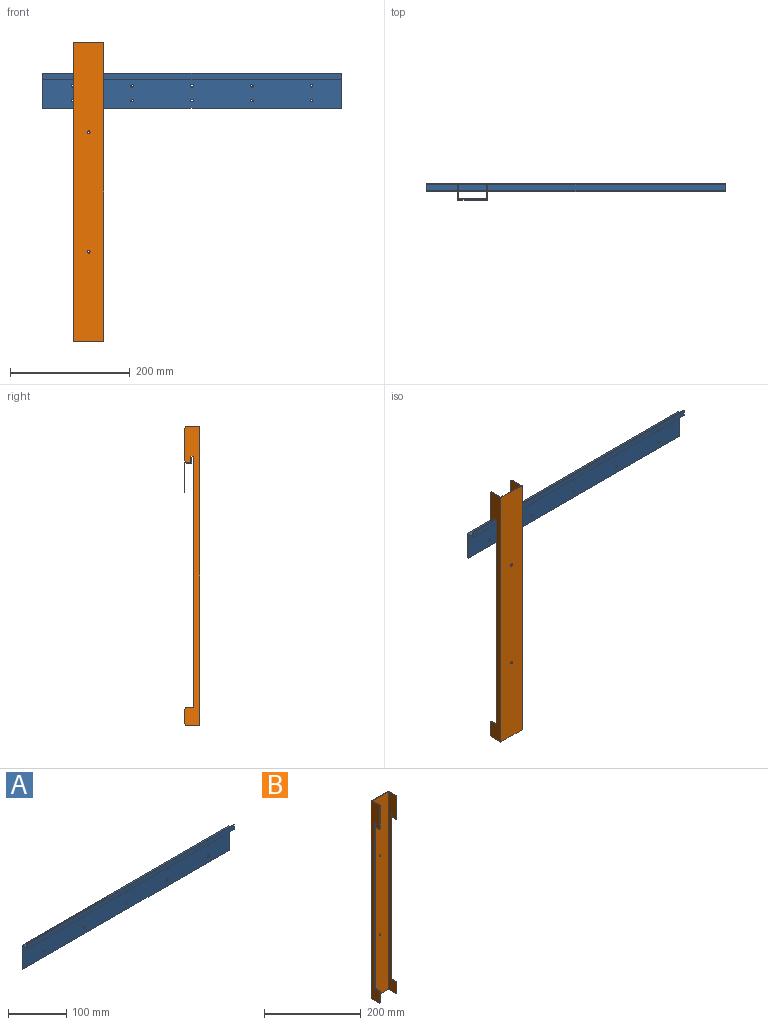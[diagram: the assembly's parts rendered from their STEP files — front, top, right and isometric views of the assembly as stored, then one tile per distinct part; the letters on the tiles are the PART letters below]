
ASSEMBLY  parts=2 mates=1
PART A: 20 faces, bbox 500x13x58.5 mm
  f0: plane 500x11.5mm, normal (0,0,1), area 5750mm2, adj f1,f3,f5,f8
  f1: plane 58.5x13mm, normal (-1,0,0), area 105mm2, adj f0,f2,f4,f5,f6,f7,f8,f9
  f2: plane 500x1.5mm, normal (0,0,-1), area 750mm2, adj f1,f3,f4,f5
  f3: plane 58.5x13mm, normal (1,0,0), area 105mm2, adj f0,f2,f4,f5,f6,f7,f8,f9
  f4: plane 500x48.5mm, normal (0,-1,0), area 24104.8mm2, adj f1,f2,f3,f6,f10,f11,f12,f13
  f5: plane 500x50mm, normal (0,1,0), area 24854.8mm2, adj f0,f1,f2,f3,f10,f11,f12,f13
  f6: plane 500x11.5mm, normal (0,0,-1), area 5750mm2, adj f1,f3,f4,f7
  f7: plane 500x10mm, normal (0,-1,0), area 5000mm2, adj f1,f3,f6,f9
  f8: plane 500x8.5mm, normal (0,1,0), area 4250mm2, adj f0,f1,f3,f9
  f9: plane 500x1.5mm, normal (0,0,1), area 750mm2, adj f1,f3,f7,f8
  f10: cylinder r=2.15mm len=4.3mm, axis (0,-1,0), area 20.3mm2, adj f4,f5
  f11: cylinder r=2.15mm len=4.3mm, axis (0,-1,0), area 20.3mm2, adj f4,f5
  f12: cylinder r=2.15mm len=4.3mm, axis (0,-1,0), area 20.3mm2, adj f4,f5
  f13: cylinder r=2.15mm len=4.3mm, axis (0,-1,0), area 20.3mm2, adj f4,f5
  f14: cylinder r=2.15mm len=4.3mm, axis (0,-1,0), area 20.3mm2, adj f4,f5
  f15: cylinder r=2.15mm len=4.3mm, axis (0,-1,0), area 20.3mm2, adj f4,f5
  f16: cylinder r=2.15mm len=4.3mm, axis (0,-1,0), area 20.3mm2, adj f4,f5
  f17: cylinder r=2.15mm len=4.3mm, axis (0,-1,0), area 20.3mm2, adj f4,f5
  f18: cylinder r=2.15mm len=4.3mm, axis (0,-1,0), area 20.3mm2, adj f4,f5
  f19: cylinder r=2.15mm len=4.3mm, axis (0,-1,0), area 20.3mm2, adj f4,f5
PART B: 32 faces, bbox 50x25x500 mm
  f0: plane 24x1.5mm, normal (0,-1,0), area 36mm2, adj f3,f8,f25,f31
  f1: plane 24x1.5mm, normal (0,-1,0), area 36mm2, adj f5,f10,f27,f28
  f2: plane 500x47mm, normal (0,-1,0), area 23472.3mm2, adj f4,f6,f8,f10,f22,f23
  f3: plane 500x25mm, normal (-1,0,0), area 6292.3mm2, adj f0,f4,f6,f7,f9,f17,f18,f19
  f4: plane 50x22mm, normal (0,0,-1), area 136.5mm2, adj f2,f3,f5,f7,f8,f10,f28,f31
  f5: plane 500x25mm, normal (1,0,0), area 6292.3mm2, adj f1,f4,f6,f7,f11,f12,f13,f14
  f6: plane 50x22mm, normal (0,0,1), area 136.5mm2, adj f2,f3,f5,f7,f8,f10,f29,f30
  f7: plane 500x50mm, normal (0,1,0), area 24972.3mm2, adj f3,f4,f5,f6,f22,f23
  f8: plane 500x23.5mm, normal (1,0,0), area 5542.3mm2, adj f0,f2,f4,f6,f9,f17,f18,f19
  f9: plane 54x1.5mm, normal (0,-1,0), area 81mm2, adj f3,f8,f24,f30
  f10: plane 500x23.5mm, normal (-1,0,0), area 5542.3mm2, adj f1,f2,f4,f6,f11,f12,f13,f14
  f11: plane 54x1.5mm, normal (0,-1,0), area 81mm2, adj f5,f10,f26,f29
  f12: plane 12x1.5mm, normal (0,0,1), area 18mm2, adj f5,f10,f13,f27
  f13: plane 420x1.5mm, normal (0,-1,0), area 630mm2, adj f5,f10,f12,f14
  f14: plane 5x1.5mm, normal (0,0,-1), area 7.5mm2, adj f5,f10,f13,f15
  f15: plane 10x1.5mm, normal (0,1,0), area 15mm2, adj f5,f10,f14,f16
  f16: plane 7x1.5mm, normal (0,0,-1), area 10.5mm2, adj f5,f10,f15,f26
  f17: plane 7x1.5mm, normal (0,0,-1), area 10.5mm2, adj f3,f8,f18,f24
  f18: plane 10x1.5mm, normal (0,1,0), area 15mm2, adj f3,f8,f17,f19
  f19: plane 5x1.5mm, normal (0,0,-1), area 7.5mm2, adj f3,f8,f18,f20
  f20: plane 420x1.5mm, normal (0,-1,0), area 630mm2, adj f3,f8,f19,f21
  f21: plane 12x1.5mm, normal (0,0,1), area 18mm2, adj f3,f8,f20,f25
  f22: cylinder r=2.1mm len=4.2mm, axis (0,-1,0), area 19.8mm2, adj f2,f7
  f23: cylinder r=2.1mm len=4.2mm, axis (0,-1,0), area 19.8mm2, adj f2,f7
  f24: cylinder r=3mm len=3mm, axis (1,0,0), area 7.1mm2, adj f3,f8,f9,f17
  f25: cylinder r=3mm len=3mm, axis (1,0,0), area 7.1mm2, adj f0,f3,f8,f21
  f26: cylinder r=3mm len=3mm, axis (1,0,0), area 7.1mm2, adj f5,f10,f11,f16
  f27: cylinder r=3mm len=3mm, axis (1,0,0), area 7.1mm2, adj f1,f5,f10,f12
  f28: cylinder r=3mm len=3mm, axis (-1,0,0), area 7.1mm2, adj f1,f4,f5,f10
  f29: cylinder r=3mm len=3mm, axis (1,0,0), area 7.1mm2, adj f5,f6,f10,f11
  f30: cylinder r=3mm len=3mm, axis (1,0,0), area 7.1mm2, adj f3,f6,f8,f9
  f31: cylinder r=3mm len=3mm, axis (-1,0,0), area 7.1mm2, adj f0,f3,f4,f8
PLACE A at identity
PLACE B rot(axis=(0,0,1),180deg) t=(-172.63,-26.52,-165.16)mm
MATE parallel B.f18 <-> A.f8  axis (0,-1,0) through (-148.38,-11.52,29.84)mm
